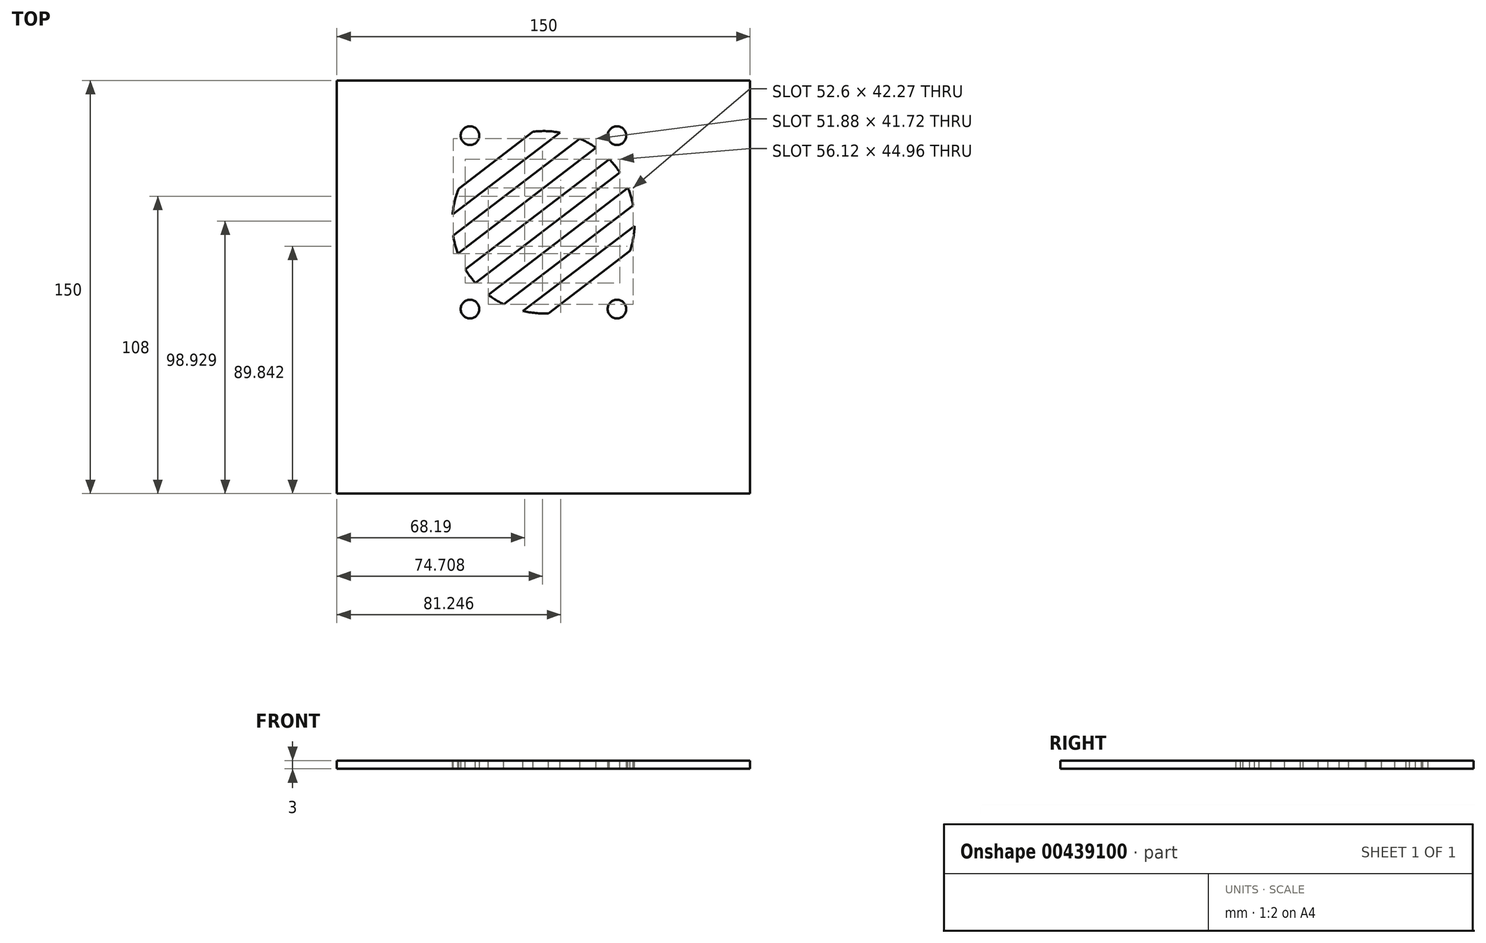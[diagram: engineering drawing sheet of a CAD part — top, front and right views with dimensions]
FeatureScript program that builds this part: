
annotation { "Feature Type Name" : "Feature", "Feature Type Description" : "" }
export const myFeature = defineFeature(function(context is Context, id is Id, definition is map)
    precondition{}
    {
        {
            var Q0;
            Q0=qCreatedBy(makeId("Top.planeOp"),FACE);
            var sketch = newSketch(context, id + "F0", { "sketchPlane" : qUnion([Q0])});
            skLineSegment(sketch, "E0.bottom", {"start": v(75, 76.92) * mm, "end": v(-75, 76.92) * mm});
            skLineSegment(sketch, "E0.top", {"start": v(75, -73.08) * mm, "end": v(-75, -73.08) * mm});
            skLineSegment(sketch, "E0.left", {"start": v(75, 76.92) * mm, "end": v(75, -73.08) * mm});
            skLineSegment(sketch, "E0.right", {"start": v(-75, 76.92) * mm, "end": v(-75, -73.08) * mm});
            skPoint(sketch, "E0.middle", {"position": v(0, 1.92) * mm});
            skCircle(sketch, "E1", {"center": v(0, 25.4) * mm, "radius": 41.28 * mm, "construction": true});
            skLineSegment(sketch, "E2.bottom", {"start": v(26.67, 56.9) * mm, "end": v(-26.67, 56.9) * mm, "construction": true});
            skLineSegment(sketch, "E2.top", {"start": v(26.67, -6.1) * mm, "end": v(-26.67, -6.1) * mm, "construction": true});
            skLineSegment(sketch, "E2.left", {"start": v(26.67, 56.9) * mm, "end": v(26.67, -6.1) * mm, "construction": true});
            skLineSegment(sketch, "E2.right", {"start": v(-26.67, 56.9) * mm, "end": v(-26.67, -6.1) * mm, "construction": true});
            skSolve(sketch);
        }
        {
            var Q0;
            Q0 = qSketchRegion(id + "F0", true);
            extrude(context, id + "F1", {"entities" : qUnion([Q0]), "depth" : 3 * mm});
        }
        {
            var Q0;
            Q0=sQuery(id+"F0.wireOp",VERTEX,"E2.right.start");
            var Q1;
            Q1=sQuery(id+"F0.wireOp",VERTEX,"E2.left.start");
            var Q2;
            Q2=sQuery(id+"F0.wireOp",VERTEX,"E2.right.end");
            var Q3;
            Q3=sQuery(id+"F0.wireOp",VERTEX,"E2.left.end");
            var Q4;
            Q4=makeQuery(id+"F1.opExtrude","SWEPT_BODY",BODY,{"disambiguationData":[OSD([sQuery(id+"F0.wireOp",EDGE,"E0.bottom"),sQuery(id+"F0.wireOp",EDGE,"E0.top"),sQuery(id+"F0.wireOp",EDGE,"E0.left"),sQuery(id+"F0.wireOp",EDGE,"E0.right")])]});
            hole(context, id + "F2", {"style" : HoleStyle.SIMPLE, "endStyle" : HoleEndStyle.THROUGH, "oppositeDirection" : true, "standardTappedOrClearance" : lookupTablePath({ "standard" : "ANSI", "fit" : "Normal (ASME)", "size" : "1/4", "type" : "Clearance" }), "standardBlindInLast" : lookupTablePath({ "fit" : "Free", "standard" : "ANSI", "size" : "1/4", "type" : "Clearance" }), "holeDiameter" : 6.76 * mm, "isTappedThrough" : true, "tappedDepth" : 12 * mm, "tapClearance" : 3, "startFromSketch" : true, "locations" : qUnion([Q0, Q1, Q2, Q3]), "scope" : qUnion([Q4])});
        }
        {
            var Q0;
            Q0=makeQuery(id+"F1.opExtrude","CAP_FACE",FACE,{"disambiguationData":[OSD([sQuery(id+"F0.wireOp",EDGE,"E0.bottom"),sQuery(id+"F0.wireOp",EDGE,"E0.top"),sQuery(id+"F0.wireOp",EDGE,"E0.left"),sQuery(id+"F0.wireOp",EDGE,"E0.right")])],"isStart":false});
            var sketch = newSketch(context, id + "F3", { "sketchPlane" : qUnion([Q0])});
            skArc(sketch, "E3", {"start": v(-30.75, 37.72) * mm, "mid": v(-32.22, 33.05) * mm, "end": v(-33, 28.2) * mm});
            skLineSegment(sketch, "E4", {"start": v(-30.75, 37.72) * mm, "end": v(-3.8, 58.33) * mm});
            skLineSegment(sketch, "E5.1.0.0", {"start": v(-33, 28.2) * mm, "end": v(5.98, 58) * mm});
            skLineSegment(sketch, "E5.2.0.0", {"start": v(-32.75, 20.6) * mm, "end": v(13.26, 55.78) * mm});
            skLineSegment(sketch, "E5.3.0.0", {"start": v(-31.09, 14.06) * mm, "end": v(19.13, 52.47) * mm});
            skLineSegment(sketch, "E5.4.0.0", {"start": v(-28.35, 8.35) * mm, "end": v(23.92, 48.33) * mm});
            skLineSegment(sketch, "E5.5.0.0", {"start": v(-24.67, 3.37) * mm, "end": v(27.77, 43.47) * mm});
            skLineSegment(sketch, "E5.6.0.0", {"start": v(-20.05, -0.9) * mm, "end": v(30.68, 37.9) * mm});
            skLineSegment(sketch, "E5.7.0.0", {"start": v(-14.4, -4.37) * mm, "end": v(32.55, 31.52) * mm});
            skLineSegment(sketch, "E5.8.0.0", {"start": v(-7.4, -6.83) * mm, "end": v(33.08, 24.13) * mm});
            skLineSegment(sketch, "E5.9.0.0", {"start": v(1.76, -7.62) * mm, "end": v(31.44, 15.08) * mm});
            skLineSegment(sketch, "E5.direction1", {"start": v(-92.23, -9.3) * mm, "end": v(-82.03, -9.3) * mm, "construction": true});
            skPoint(sketch, "E6.orphan", {"position": v(-71.83, -9.3) * mm});
            skPoint(sketch, "E7.orphan", {"position": v(-61.63, -9.3) * mm});
            skPoint(sketch, "E8.orphan", {"position": v(-51.43, -9.3) * mm});
            skPoint(sketch, "E9.orphan", {"position": v(-41.23, -9.3) * mm});
            skPoint(sketch, "E10.orphan", {"position": v(-31.03, -9.3) * mm});
            skPoint(sketch, "E11.orphan", {"position": v(-20.83, -9.3) * mm});
            skPoint(sketch, "E12.orphan", {"position": v(-10.63, -9.3) * mm});
            skPoint(sketch, "E13.orphan", {"position": v(-0.43, -9.3) * mm});
            skPoint(sketch, "E14.orphan", {"position": v(3.44, 63.87) * mm});
            skPoint(sketch, "E15.orphan", {"position": v(13.64, 63.87) * mm});
            skPoint(sketch, "E16.orphan", {"position": v(23.84, 63.87) * mm});
            skPoint(sketch, "E17.orphan", {"position": v(34.04, 63.87) * mm});
            skPoint(sketch, "E18.orphan", {"position": v(44.24, 63.87) * mm});
            skPoint(sketch, "E19.orphan", {"position": v(54.44, 63.87) * mm});
            skPoint(sketch, "E20.orphan", {"position": v(64.64, 63.87) * mm});
            skPoint(sketch, "E21.orphan", {"position": v(74.84, 63.87) * mm});
            skPoint(sketch, "E22.orphan", {"position": v(85.04, 63.87) * mm});
            skPoint(sketch, "E23.orphan", {"position": v(95.24, 63.87) * mm});
            skArc(sketch, "E24.trimOffspring", {"start": v(-32.75, 20.6) * mm, "mid": v(-32.09, 17.28) * mm, "end": v(-31.09, 14.06) * mm});
            skArc(sketch, "E25.trimOffspring", {"start": v(5.98, 58) * mm, "mid": v(1.1, 58.53) * mm, "end": v(-3.8, 58.33) * mm});
            skArc(sketch, "E26.trimOffspring", {"start": v(19.13, 52.47) * mm, "mid": v(16.28, 54.27) * mm, "end": v(13.26, 55.78) * mm});
            skArc(sketch, "E27.trimOffspring", {"start": v(-28.35, 8.35) * mm, "mid": v(-26.63, 5.77) * mm, "end": v(-24.67, 3.37) * mm});
            skArc(sketch, "E28.trimOffspring", {"start": v(27.77, 43.47) * mm, "mid": v(25.96, 46) * mm, "end": v(23.92, 48.33) * mm});
            skArc(sketch, "E29.trimOffspring", {"start": v(-20.05, -0.9) * mm, "mid": v(-17.3, -2.78) * mm, "end": v(-14.4, -4.37) * mm});
            skArc(sketch, "E30.trimOffspring", {"start": v(-7.4, -6.83) * mm, "mid": v(-2.85, -7.54) * mm, "end": v(1.76, -7.62) * mm});
            skArc(sketch, "E31.trimOffspring", {"start": v(32.55, 31.52) * mm, "mid": v(31.77, 34.76) * mm, "end": v(30.68, 37.9) * mm});
            skArc(sketch, "E32.trimOffspring", {"start": v(31.44, 15.08) * mm, "mid": v(32.58, 19.55) * mm, "end": v(33.08, 24.13) * mm});
            skSolve(sketch);
        }
        {
            var Q0;
            Q0 = qSketchRegion(id + "F3", true);
            extrude(context, id + "F4", {"entities" : qUnion([Q0]), "operationType" : NewBodyOperationType.REMOVE, "oppositeDirection" : true, "depth" : 25 * mm});
        }
    });
